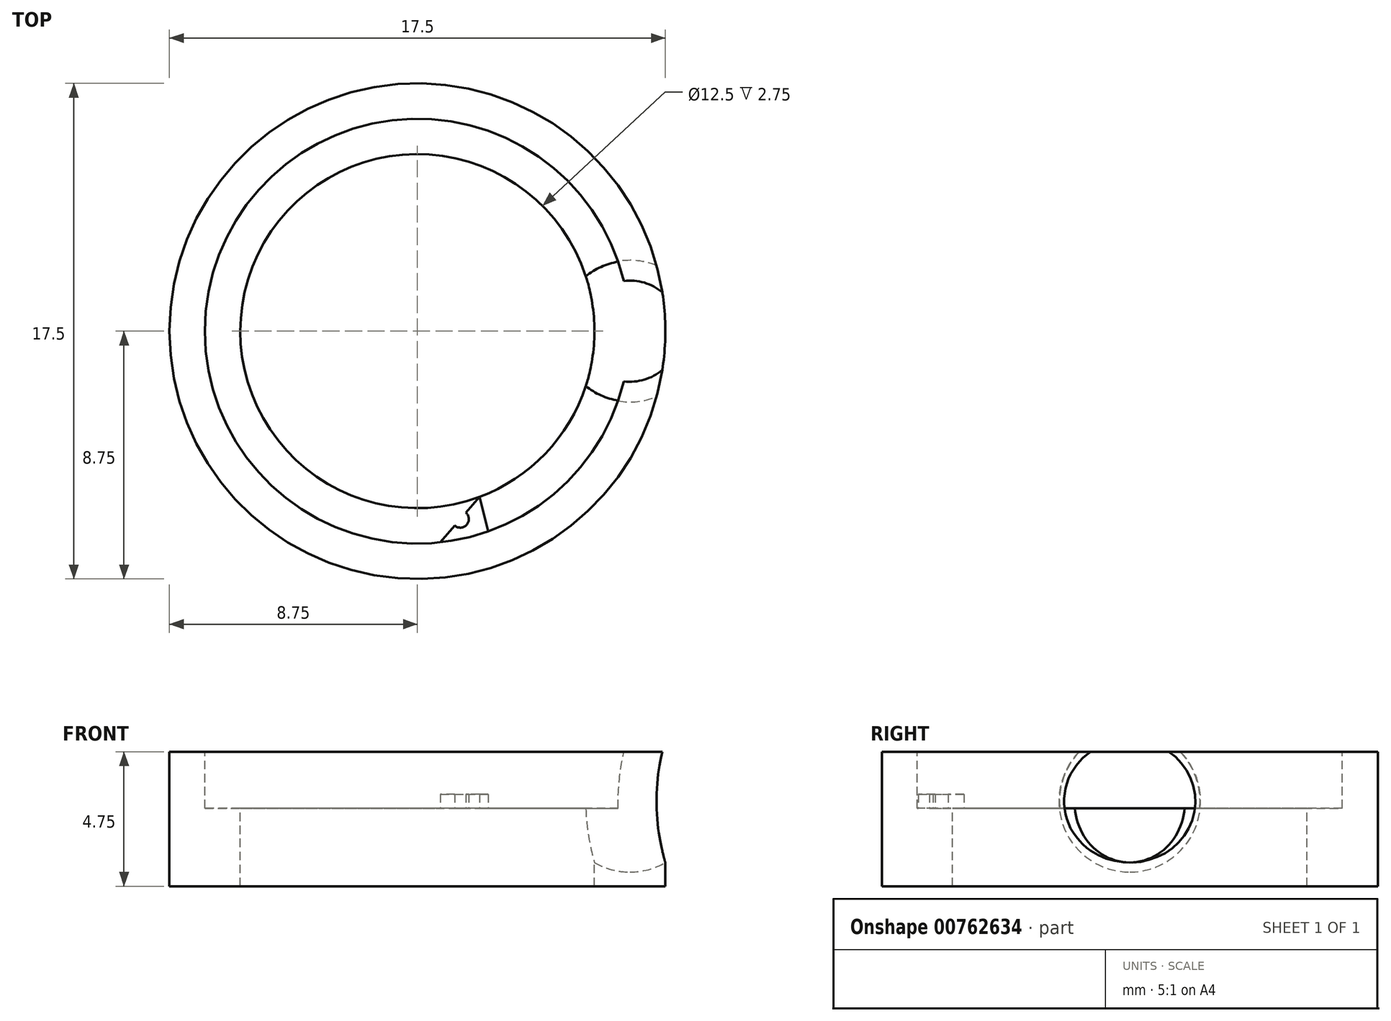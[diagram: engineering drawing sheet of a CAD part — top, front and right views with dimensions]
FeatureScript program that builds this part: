
annotation { "Feature Type Name" : "Feature", "Feature Type Description" : "" }
export const myFeature = defineFeature(function(context is Context, id is Id, definition is map)
    precondition{}
    {
        {
            var Q0;
            Q0=qCreatedBy(makeId("Front.planeOp"),FACE);
            var sketch = newSketch(context, id + "F0", { "sketchPlane" : qUnion([Q0])});
            skLineSegment(sketch, "E0", {"start": v(0, 9.66) * mm, "end": v(0, -12.64) * mm});
            skLineSegment(sketch, "E1", {"start": v(6.25, 0) * mm, "end": v(8.75, 0) * mm});
            skLineSegment(sketch, "E2", {"start": v(6.25, -3.5) * mm, "end": v(8.75, -3.5) * mm});
            skLineSegment(sketch, "E3", {"start": v(8.75, 3.5) * mm, "end": v(6.25, 3.5) * mm});
            skLineSegment(sketch, "E4.0", {"start": v(6.25, 0) * mm, "end": v(6.25, -3.5) * mm});
            skLineSegment(sketch, "E4.1", {"start": v(6.25, 3.5) * mm, "end": v(6.25, 0) * mm});
            skPoint(sketch, "E5.orphan", {"position": v(9, -3.5) * mm});
            skPoint(sketch, "E6.orphan", {"position": v(6, 0) * mm});
            skPoint(sketch, "E7.orphan", {"position": v(6, 3.5) * mm});
            skLineSegment(sketch, "E8.0", {"start": v(8.75, -3.5) * mm, "end": v(8.75, 3.5) * mm});
            skPoint(sketch, "E9.orphan", {"position": v(9, 0) * mm});
            skSolve(sketch);
        }
        {
            var Q0;
            Q0=qSketchRegion(id+"F0",true);
            var Q1;
            Q1=sQuery(id+"F0.wireOp",EDGE,"E0");
            revolve(context, id + "F1", {"surfaceOperationType" : NewSurfaceOperationType.NEW, "entities" : qUnion([Q0]), "axis" : qUnion([Q1]), "revolveType" : RevolveType.FULL});
        }
        {
            var Q0;
            Q0=qCreatedBy(makeId("Front.planeOp"),FACE);
            var sketch = newSketch(context, id + "F2", { "sketchPlane" : qUnion([Q0])});
            skLineSegment(sketch, "E10", {"start": v(0, 0) * mm, "end": v(6.25, 0) * mm});
            skLineSegment(sketch, "E11", {"start": v(6.25, 0) * mm, "end": v(6.25, 0) * mm});
            skLineSegment(sketch, "E12", {"start": v(6.25, 0) * mm, "end": v(8.75, 0) * mm});
            skCircle(sketch, "E13", {"center": v(7.5, 0) * mm, "radius": 2.5 * mm});
            skLineSegment(sketch, "E14", {"start": v(7.5, 2.5) * mm, "end": v(7.5, -2.5) * mm});
            skSolve(sketch);
        }
        {
            var Q0;
            {var subQ0=sQuery(id+"F2.wireOp",EDGE,"E14");var subQ1=sQuery(id+"F2.wireOp",EDGE,"E13");var subQ2=makeQuery(id+"F2.imprint","INTERSECT",VERTEX,{"disambiguationData":[OD(0.0)],"derivedFrom":[subQ1,subQ0]});Q0=makeQuery(id+"F2.imprint","IMPRINT",FACE,{"disambiguationData":[TD([[makeQuery(id+"F2.imprint","IMPRINT",EDGE,{"disambiguationData":[TD([[subQ2,1.0]])],"derivedFrom":subQ1}),1.0]])]});}
            var Q1;
            Q1=sQuery(id+"F2.wireOp",EDGE,"E14");
            revolve(context, id + "F3", {"operationType" : NewBodyOperationType.REMOVE, "surfaceOperationType" : NewSurfaceOperationType.NEW, "entities" : qUnion([Q0]), "axis" : qUnion([Q1]), "revolveType" : RevolveType.FULL, "oppositeDirection" : true});
        }
        {
            var Q0;
            Q0=qCreatedBy(makeId("Front.planeOp"),FACE);
            var sketch = newSketch(context, id + "F4", { "sketchPlane" : qUnion([Q0])});
            skLineSegment(sketch, "E15", {"start": v(0, 8.37) * mm, "end": v(0, -14.66) * mm});
            skSolve(sketch);
        }
        {
            var Q0;
            Q0=qCreatedBy(makeId("Front.planeOp"),FACE);
            var sketch = newSketch(context, id + "F5", { "sketchPlane" : qUnion([Q0])});
            skLineSegment(sketch, "E16", {"start": v(0, 0) * mm, "end": v(0, 1.75) * mm});
            skLineSegment(sketch, "E17", {"start": v(0, 1.75) * mm, "end": v(-9, 1.75) * mm});
            skLineSegment(sketch, "E18.bottom", {"start": v(-9, 1.75) * mm, "end": v(9.16, 1.75) * mm});
            skLineSegment(sketch, "E18.top", {"start": v(-9, 4.49) * mm, "end": v(9.16, 4.49) * mm});
            skLineSegment(sketch, "E18.left", {"start": v(-9, 1.75) * mm, "end": v(-9, 4.49) * mm});
            skLineSegment(sketch, "E18.right", {"start": v(9.16, 1.75) * mm, "end": v(9.16, 4.49) * mm});
            skLineSegment(sketch, "E19", {"start": v(0, 0) * mm, "end": v(0, -3) * mm});
            skLineSegment(sketch, "E20.bottom", {"start": v(-9.2, -3) * mm, "end": v(9.16, -3) * mm});
            skLineSegment(sketch, "E20.top", {"start": v(-9.2, -4.73) * mm, "end": v(9.16, -4.73) * mm});
            skLineSegment(sketch, "E20.left", {"start": v(-9.2, -3) * mm, "end": v(-9.2, -4.73) * mm});
            skLineSegment(sketch, "E20.right", {"start": v(9.16, -3) * mm, "end": v(9.16, -4.73) * mm});
            skSolve(sketch);
        }
        {
            var Q0;
            {Q0=qUnion([makeQuery(id+"F5.imprint","IMPRINT",FACE,{"disambiguationData":[TD([[makeQuery(id+"F5.imprint","IMPRINT",EDGE,{"derivedFrom":sQuery(id+"F5.wireOp",EDGE,"E17")}),-1.0]])]}),makeQuery(id+"F5.imprint","IMPRINT",FACE,{"disambiguationData":[TD([[makeQuery(id+"F5.imprint","IMPRINT",EDGE,{"derivedFrom":sQuery(id+"F5.wireOp",EDGE,"E20.top")}),1.0]])]})]);}
            extrude(context, id + "F6", {"entities" : qUnion([Q0]), "operationType" : NewBodyOperationType.REMOVE, "endBound" : BoundingType.SYMMETRIC, "oppositeDirection" : true, "depth" : 25 * mm, "offsetDistance" : 25 * mm});
        }
        {
            var Q0;
            {var subQ0=sQuery(id+"F2.wireOp",EDGE,"E13");Q0=makeQuery(id+"F6.boolean.opBoolean","COPY",FACE,{"disambiguationData":[TD([makeQuery(id+"F1.opRevolve","SWEPT_FACE",FACE,{"disambiguationData":[OSD([sQuery(id+"F0.wireOp",EDGE,"E4.0"),sQuery(id+"F0.wireOp",EDGE,"E4.1")])]}),makeQuery(id+"F1.opRevolve","SWEPT_FACE",FACE,{"disambiguationData":[OSD([sQuery(id+"F0.wireOp",EDGE,"E8.0")])]}),makeQuery(id+"F6Gl4txAeZpl2Zy_1.1.F3.boolean.opBoolean","COPY",FACE,{"derivedFrom":makeQuery(id+"F6Gl4txAeZpl2Zy_1.1.F3.opRevolve","SWEPT_FACE",FACE,{"disambiguationData":[OSD([subQ0])]})}),makeQuery(id+"F6Gl4txAeZpl2Zy_1.2.F3.boolean.opBoolean","COPY",FACE,{"derivedFrom":makeQuery(id+"F6Gl4txAeZpl2Zy_1.2.F3.opRevolve","SWEPT_FACE",FACE,{"disambiguationData":[OSD([subQ0])]})})])],"derivedFrom":makeQuery(id+"F6.opExtrude","SWEPT_FACE",FACE,{"disambiguationData":[OSD([sQuery(id+"F5.wireOp",EDGE,"E17"),sQuery(id+"F5.wireOp",EDGE,"E18.bottom")])]})});}
            var sketch = newSketch(context, id + "F7", { "sketchPlane" : qUnion([Q0])});
            skCircle(sketch, "E21", {"center": v(0, 0) * mm, "radius": 7.5 * mm});
            skSolve(sketch);
        }
        {
            var Q0;
            Q0=qSketchRegion(id+"F7",true);
            extrude(context, id + "F8", {"entities" : qUnion([Q0]), "operationType" : NewBodyOperationType.REMOVE, "oppositeDirection" : true, "depth" : 2 * mm, "offsetDistance" : 25 * mm});
        }
        {
            var Q0;
            {var subQ0=sQuery(id+"F2.wireOp",EDGE,"E13");var subQ1=sQuery(id+"F7.wireOp",EDGE,"E21");Q0=makeQuery(id+"F8.boolean.opBoolean","COPY",FACE,{"disambiguationData":[TD([makeQuery(id+"F1.opRevolve","SWEPT_FACE",FACE,{"disambiguationData":[OSD([sQuery(id+"F0.wireOp",EDGE,"E4.0"),sQuery(id+"F0.wireOp",EDGE,"E4.1")])]}),makeQuery(id+"F6Gl4txAeZpl2Zy_1.1.F3.boolean.opBoolean","COPY",FACE,{"derivedFrom":makeQuery(id+"F6Gl4txAeZpl2Zy_1.1.F3.opRevolve","SWEPT_FACE",FACE,{"disambiguationData":[OSD([subQ0])]})}),makeQuery(id+"F6Gl4txAeZpl2Zy_1.2.F3.boolean.opBoolean","COPY",FACE,{"derivedFrom":makeQuery(id+"F6Gl4txAeZpl2Zy_1.2.F3.opRevolve","SWEPT_FACE",FACE,{"disambiguationData":[OSD([subQ0])]})}),makeQuery(id+"F8.opExtrude","SWEPT_FACE",FACE,{"disambiguationData":[OSD([subQ1])]})])],"derivedFrom":makeQuery(id+"F8.opExtrude","CAP_FACE",FACE,{"disambiguationData":[OSD([subQ1])],"isStart":false})});}
            var sketch = newSketch(context, id + "F9", { "sketchPlane" : qUnion([Q0])});
            skLineSegment(sketch, "E22", {"start": v(0.57, -6.22) * mm, "end": v(2.5, -7.07) * mm});
            skLineSegment(sketch, "E23", {"start": v(2.5, -7.07) * mm, "end": v(2.19, -5.85) * mm});
            skLineSegment(sketch, "E24", {"start": v(2.19, -5.85) * mm, "end": v(0.81, -7.46) * mm});
            skLineSegment(sketch, "E25", {"start": v(0.81, -7.46) * mm, "end": v(0.57, -6.22) * mm});
            skCircle(sketch, "E26", {"center": v(1.52, -6.64) * mm, "radius": 0.4 * mm});
            skCircle(sketch, "E27", {"center": v(1.52, -6.64) * mm, "radius": 0.3 * mm});
            skSolve(sketch);
        }
        {
            var Q0;
            {var subQ0=sQuery(id+"F9.wireOp",EDGE,"E26");var subQ1=sQuery(id+"F9.wireOp",EDGE,"E22");var subQ2=makeQuery(id+"F9.imprint","INTERSECT",VERTEX,{"disambiguationData":[OD(0.0)],"derivedFrom":[subQ1,subQ0]});Q0=makeQuery(id+"F9.imprint","IMPRINT",FACE,{"disambiguationData":[TD([[makeQuery(id+"F9.imprint","IMPRINT",EDGE,{"disambiguationData":[TD([[subQ2,-1.0]])],"derivedFrom":subQ1}),1.0]])]});}
            var Q1;
            {var subQ0=sQuery(id+"F9.wireOp",EDGE,"E27");var subQ1=sQuery(id+"F9.wireOp",EDGE,"E22");var subQ2=makeQuery(id+"F9.imprint","INTERSECT",VERTEX,{"disambiguationData":[OD(1.0)],"derivedFrom":[subQ1,subQ0]});Q1=makeQuery(id+"F9.imprint","IMPRINT",FACE,{"disambiguationData":[TD([[makeQuery(id+"F9.imprint","IMPRINT",EDGE,{"disambiguationData":[TD([[subQ2,-1.0]])],"derivedFrom":subQ1}),1.0]])]});}
            var Q2;
            {var subQ0=sQuery(id+"F9.wireOp",EDGE,"E27");var subQ1=sQuery(id+"F9.wireOp",EDGE,"E22");var subQ2=makeQuery(id+"F9.imprint","INTERSECT",VERTEX,{"disambiguationData":[OD(1.0)],"derivedFrom":[subQ1,subQ0]});Q2=makeQuery(id+"F9.imprint","IMPRINT",FACE,{"disambiguationData":[TD([[makeQuery(id+"F9.imprint","IMPRINT",EDGE,{"disambiguationData":[TD([[subQ2,-1.0]])],"derivedFrom":subQ1}),-1.0]])]});}
            var Q3;
            {var subQ0=sQuery(id+"F9.wireOp",EDGE,"E26");var subQ1=sQuery(id+"F9.wireOp",EDGE,"E22");var subQ2=makeQuery(id+"F9.imprint","INTERSECT",VERTEX,{"disambiguationData":[OD(0.0)],"derivedFrom":[subQ1,subQ0]});Q3=makeQuery(id+"F9.imprint","IMPRINT",FACE,{"disambiguationData":[TD([[makeQuery(id+"F9.imprint","IMPRINT",EDGE,{"disambiguationData":[TD([[subQ2,-1.0]])],"derivedFrom":subQ1}),-1.0]])]});}
            extrude(context, id + "F10", {"entities" : qUnion([Q0, Q1, Q2, Q3]), "operationType" : NewBodyOperationType.ADD, "depth" : 0.5 * mm, "offsetDistance" : 25 * mm});
        }
        {
            var Q0;
            Q0=qCreatedBy(makeId("Front.planeOp"),FACE);
            var sketch = newSketch(context, id + "F11", { "sketchPlane" : qUnion([Q0])});
            skLineSegment(sketch, "E28", {"start": v(0, 4.8) * mm, "end": v(0, -5.9) * mm});
            skSolve(sketch);
        }
    });
